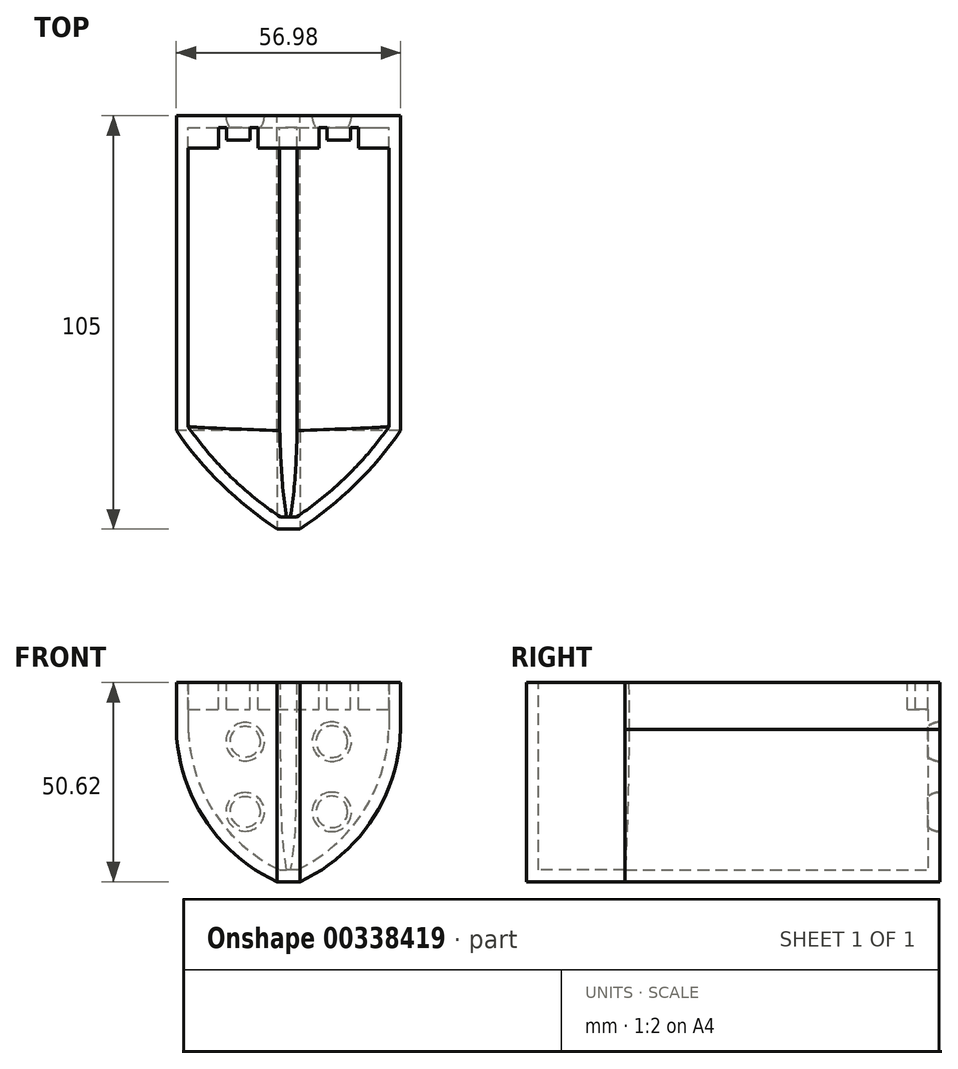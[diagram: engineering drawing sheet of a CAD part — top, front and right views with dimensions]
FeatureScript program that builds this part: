
annotation { "Feature Type Name" : "Feature", "Feature Type Description" : "" }
export const myFeature = defineFeature(function(context is Context, id is Id, definition is map)
    precondition{}
    {
        {
            var Q0;
            Q0=qCreatedBy(makeId("Front.planeOp"),FACE);
            var sketch = newSketch(context, id + "F0", { "sketchPlane" : qUnion([Q0])});
            skLineSegment(sketch, "E0.bottom", {"start": v(0, 23.95) * mm, "end": v(-28.49, 23.95) * mm});
            skLineSegment(sketch, "E0.top", {"start": v(0, -26.67) * mm, "end": v(-2.9, -26.67) * mm});
            skLineSegment(sketch, "E0.right", {"start": v(-28.49, 23.95) * mm, "end": v(-28.49, 11.98) * mm});
            skArc(sketch, "E1", {"start": v(-28.49, 11.98) * mm, "mid": v(-21.19, -10.99) * mm, "end": v(-2.9, -26.67) * mm});
            skArc(sketch, "E2.MirrorCS", {"start": v(28.49, 11.98) * mm, "mid": v(21.19, -10.99) * mm, "end": v(2.9, -26.67) * mm});
            skLineSegment(sketch, "E3.MirrorCS", {"start": v(28.49, 23.95) * mm, "end": v(28.49, 11.98) * mm});
            skLineSegment(sketch, "E4.MirrorCS", {"start": v(0, 23.95) * mm, "end": v(28.49, 23.95) * mm});
            skLineSegment(sketch, "E5.MirrorCS", {"start": v(0, -26.67) * mm, "end": v(2.9, -26.67) * mm});
            skPoint(sketch, "E6.orphan", {"position": v(-28.49, -26.67) * mm});
            skPoint(sketch, "E7.orphan", {"position": v(28.49, -26.67) * mm});
            skLineSegment(sketch, "E8", {"start": v(21.64, -14.65) * mm, "end": v(2.2, -27.87) * mm, "construction": true});
            skLineSegment(sketch, "E9", {"start": v(21.64, -14.65) * mm, "end": v(1.77, -14.65) * mm, "construction": true});
            skLineSegment(sketch, "E10", {"start": v(31.87, 5.15) * mm, "end": v(21.19, -10.99) * mm, "construction": true});
            skLineSegment(sketch, "E11", {"start": v(31.87, 5.15) * mm, "end": v(15.11, 5.15) * mm, "construction": true});
            skLineSegment(sketch, "E12", {"start": v(-28.5, 7.24) * mm, "end": v(-28.5, -18.6) * mm, "construction": true});
            skLineSegment(sketch, "E13", {"start": v(-28.22, 4.49) * mm, "end": v(-22.81, -9.74) * mm, "construction": true});
            skLineSegment(sketch, "E14", {"start": v(-8.8, -26.7) * mm, "end": v(-17.82, -15.48) * mm, "construction": true});
            skLineSegment(sketch, "E15", {"start": v(-2.86, -26.79) * mm, "end": v(-16.68, -19.38) * mm, "construction": true});
            skSolve(sketch);
        }
        {
            var Q0;
            Q0=makeQuery(id+"F0.imprint","IMPRINT",FACE,{"disambiguationData":[TD([[makeQuery(id+"F0.imprint","IMPRINT",EDGE,{"derivedFrom":sQuery(id+"F0.wireOp",EDGE,"E0.bottom")}),1.0]])]});
            extrude(context, id + "F1", {"entities" : qUnion([Q0]), "depth" : 80 * mm});
        }
        {
            var Q0;
            Q0=makeQuery(id+"F1.opExtrude","CAP_FACE",FACE,{"disambiguationData":[OSD([sQuery(id+"F0.wireOp",EDGE,"E0.bottom"),sQuery(id+"F0.wireOp",EDGE,"E0.top"),sQuery(id+"F0.wireOp",EDGE,"E0.right"),sQuery(id+"F0.wireOp",EDGE,"E1"),sQuery(id+"F0.wireOp",EDGE,"E2.MirrorCS"),sQuery(id+"F0.wireOp",EDGE,"E3.MirrorCS"),sQuery(id+"F0.wireOp",EDGE,"E4.MirrorCS"),sQuery(id+"F0.wireOp",EDGE,"E5.MirrorCS")])],"isStart":false});
            cPlane(context, id + "F2", {"entities" : qUnion([Q0]), "cplaneType" : CPlaneType.OFFSET, "offset" : 25 * mm, "width" : 150 * mm, "height" : 150 * mm});
        }
        {
            var Q0;
            Q0=qCreatedBy(id+"F2.planeOp",FACE);
            var sketch = newSketch(context, id + "F3", { "sketchPlane" : qUnion([Q0])});
            skLineSegment(sketch, "E16.bottom", {"start": v(0, -26.67) * mm, "end": v(-2.9, -26.67) * mm});
            skLineSegment(sketch, "E16.top", {"start": v(0, 23.95) * mm, "end": v(-2.9, 23.95) * mm});
            skLineSegment(sketch, "E16.right", {"start": v(-2.9, -26.67) * mm, "end": v(-2.9, 23.95) * mm});
            skLineSegment(sketch, "E17.MirrorCS", {"start": v(2.9, -26.67) * mm, "end": v(2.9, 23.95) * mm});
            skLineSegment(sketch, "E18.MirrorCS", {"start": v(0, -26.67) * mm, "end": v(2.9, -26.67) * mm});
            skLineSegment(sketch, "E19.MirrorCS", {"start": v(0, 23.95) * mm, "end": v(2.9, 23.95) * mm});
            skSolve(sketch);
        }
        {
            var Q0;
            Q0=makeQuery(id+"F1.opExtrude","SWEPT_FACE",FACE,{"disambiguationData":[OSD([sQuery(id+"F0.wireOp",EDGE,"E0.bottom"),sQuery(id+"F0.wireOp",EDGE,"E4.MirrorCS")])]});
            cPlane(context, id + "F4", {"entities" : qUnion([Q0]), "cplaneType" : CPlaneType.OFFSET, "offset" : 0 * mm, "width" : 150 * mm, "height" : 150 * mm});
        }
        {
            var Q0;
            Q0=qCreatedBy(id+"F4.planeOp",FACE);
            var sketch = newSketch(context, id + "F5", { "sketchPlane" : qUnion([Q0])});
            skArc(sketch, "E20", {"start": v(-28.49, -80) * mm, "mid": v(-16.9, -93.73) * mm, "end": v(-2.9, -105) * mm});
            skLineSegment(sketch, "E21", {"start": v(0, -105.03) * mm, "end": v(0, -80.6) * mm, "construction": true});
            skArc(sketch, "E22.MirrorCS", {"start": v(28.49, -80) * mm, "mid": v(16.9, -93.73) * mm, "end": v(2.9, -105) * mm});
            skSolve(sketch);
        }
        {
            var Q0;
            Q0=makeQuery(id+"F1.opExtrude","SWEPT_FACE",FACE,{"disambiguationData":[OSD([sQuery(id+"F0.wireOp",EDGE,"E0.top"),sQuery(id+"F0.wireOp",EDGE,"E5.MirrorCS")])]});
            cPlane(context, id + "F6", {"entities" : qUnion([Q0]), "cplaneType" : CPlaneType.OFFSET, "offset" : 0 * mm, "width" : 150 * mm, "height" : 150 * mm});
        }
        {
            var Q0;
            Q0=qCreatedBy(id+"F6.planeOp",FACE);
            var sketch = newSketch(context, id + "F7", { "sketchPlane" : qUnion([Q0])});
            skLineSegment(sketch, "E23", {"start": v(-2.9, 80) * mm, "end": v(-2.9, 105) * mm});
            skLineSegment(sketch, "E24", {"start": v(2.9, 80) * mm, "end": v(2.9, 105) * mm});
            skSolve(sketch);
        }
        {
            var Q1;
            Q1=makeQuery(id+"F1.opExtrude","CAP_FACE",FACE,{"disambiguationData":[OSD([sQuery(id+"F0.wireOp",EDGE,"E0.bottom"),sQuery(id+"F0.wireOp",EDGE,"E0.top"),sQuery(id+"F0.wireOp",EDGE,"E0.right"),sQuery(id+"F0.wireOp",EDGE,"E1"),sQuery(id+"F0.wireOp",EDGE,"E2.MirrorCS"),sQuery(id+"F0.wireOp",EDGE,"E3.MirrorCS"),sQuery(id+"F0.wireOp",EDGE,"E4.MirrorCS"),sQuery(id+"F0.wireOp",EDGE,"E5.MirrorCS")])],"isStart":false});
            var Q2;
            Q2=makeQuery(id+"F3.imprint","IMPRINT",FACE,{"disambiguationData":[TD([[makeQuery(id+"F3.imprint","IMPRINT",EDGE,{"derivedFrom":sQuery(id+"F3.wireOp",EDGE,"E16.bottom")}),-1.0]])]});
            var Q3;
            Q3=sQuery(id+"F5.wireOp",EDGE,"E20");
            var Q4;
            Q4=sQuery(id+"F5.wireOp",EDGE,"E22.MirrorCS");
            var Q5;
            Q5=sQuery(id+"F7.wireOp",EDGE,"E24");
            var Q6;
            Q6=sQuery(id+"F7.wireOp",EDGE,"E23");
            loft(context, id + "F8", {"operationType" : NewBodyOperationType.ADD, "addGuides" : true, "sheetProfilesArray" : [{ "sheetProfileEntities" : qUnion([Q1]) }, { "sheetProfileEntities" : qUnion([Q2]) }], "guidesArray" : [{ "guideEntities" : qUnion([Q3]), "guideDerivativeType" : LoftGuideDerivativeType.DEFAULT, "guideDerivativeMagnitude" : 1 }, { "guideEntities" : qUnion([Q4]), "guideDerivativeType" : LoftGuideDerivativeType.DEFAULT, "guideDerivativeMagnitude" : 1 }, { "guideEntities" : qUnion([Q5]), "guideDerivativeType" : LoftGuideDerivativeType.DEFAULT, "guideDerivativeMagnitude" : 1 }, { "guideEntities" : qUnion([Q6]), "guideDerivativeType" : LoftGuideDerivativeType.DEFAULT, "guideDerivativeMagnitude" : 1 }]});
        }
        {
            var Q0;
            {var subQ0=sQuery(id+"F0.wireOp",EDGE,"E4.MirrorCS");var subQ1=sQuery(id+"F0.wireOp",EDGE,"E0.bottom");Q0=makeQuery(id+"F8.boolean.opBoolean","MERGE",FACE,{"derivedFrom":[makeQuery(id+"F1.opExtrude","SWEPT_FACE",FACE,{"disambiguationData":[OSD([subQ1,subQ0])]}),makeQuery(id+"F8.opLoft","SWEPT_FACE",FACE,{"disambiguationData":[OSD([subQ1,subQ0,sQuery(id+"F3.wireOp",EDGE,"E16.top"),sQuery(id+"F3.wireOp",EDGE,"E19.MirrorCS"),sQuery(id+"F5.wireOp",EDGE,"E22.MirrorCS")])]})]});}
            shell(context, id + "F9", {"entities" : qUnion([Q0]), "thickness" : 3 * mm});
        }
        {
            var Q0;
            {var subQ0=sQuery(id+"F0.wireOp",EDGE,"E4.MirrorCS");var subQ1=sQuery(id+"F0.wireOp",EDGE,"E0.bottom");Q0=makeQuery(id+"F8.boolean.opBoolean","MERGE",FACE,{"derivedFrom":[makeQuery(id+"F1.opExtrude","SWEPT_FACE",FACE,{"disambiguationData":[OSD([subQ1,subQ0])]}),makeQuery(id+"F8.opLoft","SWEPT_FACE",FACE,{"disambiguationData":[OSD([subQ1,subQ0,sQuery(id+"F3.wireOp",EDGE,"E16.top"),sQuery(id+"F3.wireOp",EDGE,"E19.MirrorCS"),sQuery(id+"F5.wireOp",EDGE,"E22.MirrorCS")])]})]});}
            var sketch = newSketch(context, id + "F10", { "sketchPlane" : qUnion([Q0])});
            skLineSegment(sketch, "E25.bottom", {"start": v(-25.49, -3) * mm, "end": v(25.49, -3) * mm});
            skLineSegment(sketch, "E25.top", {"start": v(-25.49, -8.24) * mm, "end": v(25.49, -8.24) * mm});
            skLineSegment(sketch, "E25.left", {"start": v(-25.49, -3) * mm, "end": v(-25.49, -8.24) * mm});
            skLineSegment(sketch, "E25.right", {"start": v(25.49, -3) * mm, "end": v(25.49, -8.24) * mm});
            skSolve(sketch);
        }
        {
            var Q0;
            Q0=makeQuery(id+"F10.imprint","IMPRINT",FACE,{"disambiguationData":[TD([[makeQuery(id+"F10.imprint","IMPRINT",EDGE,{"derivedFrom":sQuery(id+"F10.wireOp",EDGE,"E25.bottom")}),-1.0]])]});
            extrude(context, id + "F11", {"entities" : qUnion([Q0]), "operationType" : NewBodyOperationType.ADD, "oppositeDirection" : true, "depth" : 6.8 * mm});
        }
        {
            var Q0;
            {var subQ0=sQuery(id+"F0.wireOp",EDGE,"E4.MirrorCS");var subQ1=sQuery(id+"F0.wireOp",EDGE,"E0.bottom");Q0=makeQuery(id+"F11.boolean.opBoolean","MERGE",FACE,{"derivedFrom":[makeQuery(id+"F8.boolean.opBoolean","MERGE",FACE,{"derivedFrom":[makeQuery(id+"F1.opExtrude","SWEPT_FACE",FACE,{"disambiguationData":[OSD([subQ1,subQ0])]}),makeQuery(id+"F8.opLoft","SWEPT_FACE",FACE,{"disambiguationData":[OSD([subQ1,subQ0,sQuery(id+"F3.wireOp",EDGE,"E16.top"),sQuery(id+"F3.wireOp",EDGE,"E19.MirrorCS"),sQuery(id+"F5.wireOp",EDGE,"E22.MirrorCS")])]})]}),makeQuery(id+"F11.opExtrude","CAP_FACE",FACE,{"disambiguationData":[OSD([sQuery(id+"F10.wireOp",EDGE,"E25.bottom"),sQuery(id+"F10.wireOp",EDGE,"E25.top"),sQuery(id+"F10.wireOp",EDGE,"E25.left"),sQuery(id+"F10.wireOp",EDGE,"E25.right")])],"isStart":true})]});}
            var sketch = newSketch(context, id + "F12", { "sketchPlane" : qUnion([Q0])});
            skLineSegment(sketch, "E26", {"start": v(0, 0) * mm, "end": v(0, -30.47) * mm, "construction": true});
            skPoint(sketch, "E26.endSnap0", {"position": v(0, 0) * mm});
            skLineSegment(sketch, "E27.bottom", {"start": v(-7.74, -8.24) * mm, "end": v(-17.74, -8.24) * mm});
            skLineSegment(sketch, "E27.top", {"start": v(-7.74, -3) * mm, "end": v(-9.74, -3) * mm});
            skLineSegment(sketch, "E27.left", {"start": v(-7.74, -8.24) * mm, "end": v(-7.74, -3) * mm});
            skLineSegment(sketch, "E27.right", {"start": v(-17.74, -8.24) * mm, "end": v(-17.74, -3) * mm});
            skLineSegment(sketch, "E28.top", {"start": v(-9.74, -6.24) * mm, "end": v(-15.74, -6.24) * mm});
            skLineSegment(sketch, "E28.left", {"start": v(-9.74, -3) * mm, "end": v(-9.74, -6.24) * mm});
            skLineSegment(sketch, "E28.right", {"start": v(-15.74, -3) * mm, "end": v(-15.74, -6.24) * mm});
            skLineSegment(sketch, "E29.trimOffspring", {"start": v(-15.74, -3) * mm, "end": v(-17.74, -3) * mm});
            skLineSegment(sketch, "E30.MirrorCS", {"start": v(7.74, -8.24) * mm, "end": v(7.74, -3) * mm});
            skLineSegment(sketch, "E31.MirrorCS", {"start": v(7.74, -3) * mm, "end": v(9.74, -3) * mm});
            skLineSegment(sketch, "E32.MirrorCS", {"start": v(9.74, -3) * mm, "end": v(9.74, -6.24) * mm});
            skLineSegment(sketch, "E33.MirrorCS", {"start": v(9.74, -6.24) * mm, "end": v(15.74, -6.24) * mm});
            skLineSegment(sketch, "E34.MirrorCS", {"start": v(7.74, -8.24) * mm, "end": v(17.74, -8.24) * mm});
            skLineSegment(sketch, "E35.MirrorCS", {"start": v(17.74, -8.24) * mm, "end": v(17.74, -3) * mm});
            skLineSegment(sketch, "E36.MirrorCS", {"start": v(15.74, -3) * mm, "end": v(17.74, -3) * mm});
            skLineSegment(sketch, "E37.MirrorCS", {"start": v(15.74, -3) * mm, "end": v(15.74, -6.24) * mm});
            skSolve(sketch);
        }
        {
            var Q0;
            Q0=makeQuery(id+"F12.imprint","IMPRINT",FACE,{"disambiguationData":[TD([[makeQuery(id+"F12.imprint","IMPRINT",EDGE,{"derivedFrom":sQuery(id+"F12.wireOp",EDGE,"E30.MirrorCS")}),-1.0]])]});
            var Q1;
            Q1=makeQuery(id+"F12.imprint","IMPRINT",FACE,{"disambiguationData":[TD([[makeQuery(id+"F12.imprint","IMPRINT",EDGE,{"derivedFrom":sQuery(id+"F12.wireOp",EDGE,"E27.bottom")}),1.0]])]});
            extrude(context, id + "F13", {"entities" : qUnion([Q0, Q1]), "operationType" : NewBodyOperationType.REMOVE, "oppositeDirection" : true, "depth" : 25 * mm});
        }
        {
            var Q0;
            Q0=makeQuery(id+"F1.opExtrude","CAP_FACE",FACE,{"disambiguationData":[OSD([sQuery(id+"F0.wireOp",EDGE,"E0.bottom"),sQuery(id+"F0.wireOp",EDGE,"E0.top"),sQuery(id+"F0.wireOp",EDGE,"E0.right"),sQuery(id+"F0.wireOp",EDGE,"E1"),sQuery(id+"F0.wireOp",EDGE,"E2.MirrorCS"),sQuery(id+"F0.wireOp",EDGE,"E3.MirrorCS"),sQuery(id+"F0.wireOp",EDGE,"E4.MirrorCS"),sQuery(id+"F0.wireOp",EDGE,"E5.MirrorCS")])],"isStart":true});
            var sketch = newSketch(context, id + "F14", { "sketchPlane" : qUnion([Q0])});
            skArc(sketch, "E38", {"start": v(-11, 13.92) * mm, "mid": v(-16, 8.92) * mm, "end": v(-11, 3.92) * mm});
            skLineSegment(sketch, "E39", {"start": v(-15.08, 0) * mm, "end": v(0, 0) * mm, "construction": true});
            skLineSegment(sketch, "E40", {"start": v(0, 10.01) * mm, "end": v(0, 0) * mm, "construction": true});
            skLineSegment(sketch, "E41", {"start": v(-11, 8.92) * mm, "end": v(-11, 3.92) * mm});
            skLineSegment(sketch, "E42", {"start": v(-11, 3.92) * mm, "end": v(-11, 13.92) * mm});
            skLineSegment(sketch, "E43.MirrorCS", {"start": v(-11, -3.92) * mm, "end": v(-11, -13.92) * mm});
            skArc(sketch, "E44.MirrorCS", {"start": v(-11, -13.92) * mm, "mid": v(-16, -8.92) * mm, "end": v(-11, -3.92) * mm});
            skSolve(sketch);
        }
        {
            var Q0;
            Q0=qSketchRegion(id+"F14",true);
            var Q1;
            Q1=sQuery(id+"F14.wireOp",EDGE,"E42");
            revolve(context, id + "F15", {"operationType" : NewBodyOperationType.REMOVE, "entities" : qUnion([Q0]), "axis" : qUnion([Q1]), "revolveType" : RevolveType.FULL});
        }
        {
            var Q0;
            Q0=makeQuery(id+"F1.opExtrude","CAP_FACE",FACE,{"disambiguationData":[OSD([sQuery(id+"F0.wireOp",EDGE,"E0.bottom"),sQuery(id+"F0.wireOp",EDGE,"E0.top"),sQuery(id+"F0.wireOp",EDGE,"E0.right"),sQuery(id+"F0.wireOp",EDGE,"E1"),sQuery(id+"F0.wireOp",EDGE,"E2.MirrorCS"),sQuery(id+"F0.wireOp",EDGE,"E3.MirrorCS"),sQuery(id+"F0.wireOp",EDGE,"E4.MirrorCS"),sQuery(id+"F0.wireOp",EDGE,"E5.MirrorCS")])],"isStart":true});
            var sketch = newSketch(context, id + "F16", { "sketchPlane" : qUnion([Q0])});
            skLineSegment(sketch, "E45", {"start": v(0, 0) * mm, "end": v(-9.83, 0) * mm, "construction": true});
            skLineSegment(sketch, "E46", {"start": v(0, 0) * mm, "end": v(0, 12.17) * mm, "construction": true});
            skArc(sketch, "E47.MirrorC", {"start": v(11, 13.82) * mm, "mid": v(15.9, 8.92) * mm, "end": v(11, 4.02) * mm});
            skArc(sketch, "E48.MirrorC", {"start": v(11, -13.82) * mm, "mid": v(15.9, -8.92) * mm, "end": v(11, -4.02) * mm});
            skLineSegment(sketch, "E49", {"start": v(11, 8.92) * mm, "end": v(11, 13.82) * mm});
            skLineSegment(sketch, "E50", {"start": v(11, 13.82) * mm, "end": v(11, 4.02) * mm});
            skLineSegment(sketch, "E51", {"start": v(11, -4.02) * mm, "end": v(11, -13.82) * mm});
            skSolve(sketch);
        }
        {
            var Q0;
            Q0=qSketchRegion(id+"F16",true);
            var Q1;
            Q1=sQuery(id+"F16.wireOp",EDGE,"E50");
            revolve(context, id + "F17", {"operationType" : NewBodyOperationType.REMOVE, "entities" : qUnion([Q0]), "axis" : qUnion([Q1]), "revolveType" : RevolveType.FULL, "oppositeDirection" : true});
        }
    });
